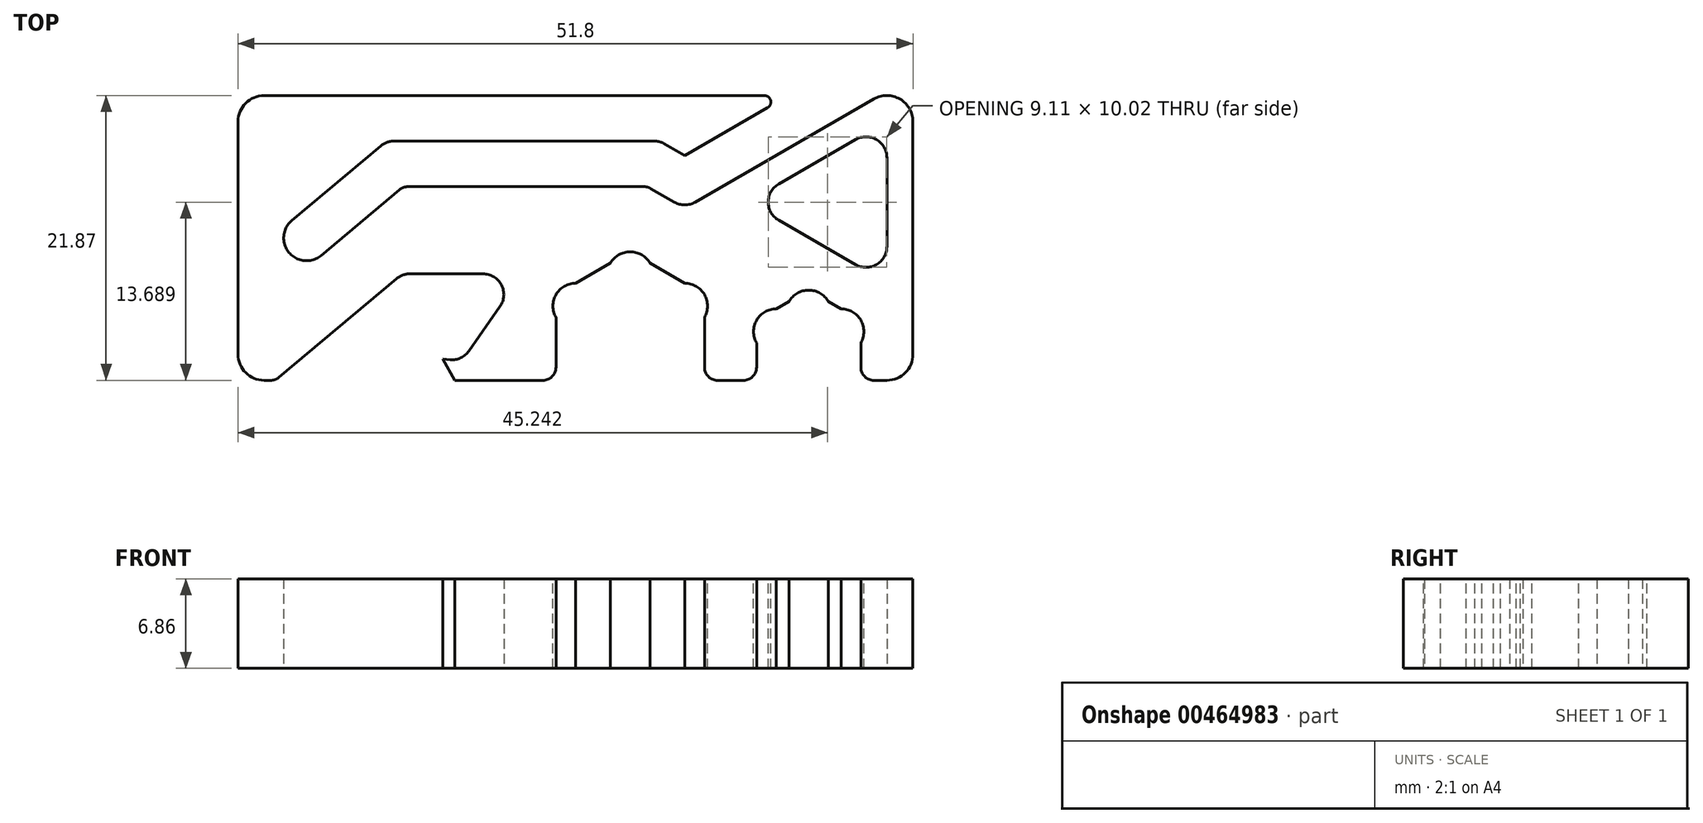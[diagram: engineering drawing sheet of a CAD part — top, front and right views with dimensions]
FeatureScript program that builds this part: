
annotation { "Feature Type Name" : "Feature", "Feature Type Description" : "" }
export const myFeature = defineFeature(function(context is Context, id is Id, definition is map)
    precondition{}
    {
        {
            var Q0;
            Q0=qCreatedBy(makeId("Top.planeOp"),FACE);
            var sketch = newSketch(context, id + "F0", { "sketchPlane" : qUnion([Q0])});
            skLineSegment(sketch, "E0", {"start": v(2, 0) * mm, "end": v(2.5, 0) * mm});
            skLineSegment(sketch, "E1", {"start": v(3.14, 0.23) * mm, "end": v(12.61, 8.18) * mm});
            skLineSegment(sketch, "E2", {"start": v(12.61, 8.18) * mm, "end": v(18.8, 8.18) * mm});
            skLineSegment(sketch, "E3", {"start": v(24.4, 0) * mm, "end": v(16.64, 0) * mm});
            skLineSegment(sketch, "E4", {"start": v(16.64, 0) * mm, "end": v(15.7, 1.63) * mm});
            skLineSegment(sketch, "E5", {"start": v(15.7, 1.63) * mm, "end": v(17.2, 1.5) * mm});
            skLineSegment(sketch, "E6", {"start": v(17.2, 1.5) * mm, "end": v(20.1, 5.66) * mm});
            skArc(sketch, "E7", {"start": v(20.1, 5.66) * mm, "mid": v(20.22, 7.32) * mm, "end": v(18.8, 8.18) * mm});
            skLineSegment(sketch, "E8", {"start": v(24.4, 0) * mm, "end": v(24.4, 6.58) * mm});
            skLineSegment(sketch, "E9", {"start": v(24.4, 6.58) * mm, "end": v(30.1, 9.87) * mm});
            skLineSegment(sketch, "E10", {"start": v(30.1, 9.87) * mm, "end": v(35.8, 6.58) * mm});
            skLineSegment(sketch, "E11", {"start": v(35.8, 6.58) * mm, "end": v(35.8, 0) * mm});
            skCircle(sketch, "E12", {"center": v(30.1, 3.3) * mm, "radius": 5.7 * mm, "construction": true});
            skLineSegment(sketch, "E13", {"start": v(18.8, 6.58) * mm, "end": v(20.4, 6.58) * mm, "construction": true});
            skArc(sketch, "E14", {"start": v(2.5, 0) * mm, "mid": v(2.84, 0.06) * mm, "end": v(3.14, 0.23) * mm});
            skLineSegment(sketch, "E15", {"start": v(0, 2) * mm, "end": v(0, 21.87) * mm});
            skArc(sketch, "E16", {"start": v(0, 2) * mm, "mid": v(0.59, 0.59) * mm, "end": v(2, 0) * mm});
            skLineSegment(sketch, "E17", {"start": v(35.8, 0) * mm, "end": v(39.8, 0) * mm});
            skLineSegment(sketch, "E18", {"start": v(39.8, 0) * mm, "end": v(39.8, 4.62) * mm});
            skLineSegment(sketch, "E19", {"start": v(39.8, 4.62) * mm, "end": v(43.8, 6.93) * mm});
            skLineSegment(sketch, "E20", {"start": v(43.8, 6.93) * mm, "end": v(47.8, 4.62) * mm});
            skLineSegment(sketch, "E21", {"start": v(47.8, 4.62) * mm, "end": v(47.8, 0) * mm});
            skLineSegment(sketch, "E22", {"start": v(47.8, 0) * mm, "end": v(51.8, 0) * mm});
            skCircle(sketch, "E23", {"center": v(43.8, 2.3) * mm, "radius": 4 * mm, "construction": true});
            skLineSegment(sketch, "E24", {"start": v(39.09, 13.69) * mm, "end": v(49.8, 7.5) * mm});
            skLineSegment(sketch, "E25", {"start": v(49.8, 7.5) * mm, "end": v(49.8, 19.87) * mm});
            skLineSegment(sketch, "E26", {"start": v(49.8, 19.87) * mm, "end": v(39.09, 13.69) * mm});
            skLineSegment(sketch, "E27", {"start": v(51.8, 0) * mm, "end": v(51.8, 19.87) * mm});
            skLineSegment(sketch, "E28", {"start": v(6.37, 9.6) * mm, "end": v(12.66, 14.87) * mm});
            skLineSegment(sketch, "E29", {"start": v(12.66, 14.87) * mm, "end": v(30.1, 14.87) * mm});
            skArc(sketch, "E30", {"start": v(4.13, 12.28) * mm, "mid": v(3.9, 9.81) * mm, "end": v(6.37, 9.6) * mm});
            skLineSegment(sketch, "E31", {"start": v(4.13, 12.28) * mm, "end": v(11.39, 18.37) * mm});
            skPoint(sketch, "E32", {"position": v(3.5, 10.94) * mm});
            skLineSegment(sketch, "E33", {"start": v(11.39, 18.37) * mm, "end": v(32.37, 18.37) * mm});
            skLineSegment(sketch, "E34", {"start": v(30.1, 14.87) * mm, "end": v(31.44, 14.87) * mm});
            skLineSegment(sketch, "E35", {"start": v(31.44, 14.87) * mm, "end": v(34.29, 13.23) * mm});
            skLineSegment(sketch, "E36", {"start": v(34.29, 13.23) * mm, "end": v(48.8, 21.6) * mm});
            skLineSegment(sketch, "E37", {"start": v(42.26, 21.87) * mm, "end": v(34.29, 17.27) * mm});
            skLineSegment(sketch, "E38", {"start": v(34.29, 17.27) * mm, "end": v(32.37, 18.37) * mm});
            skLineSegment(sketch, "E39", {"start": v(42.26, 21.87) * mm, "end": v(0, 21.87) * mm});
            skLineSegment(sketch, "E40", {"start": v(0, 0) * mm, "end": v(0, 21.87) * mm, "construction": true});
            skPoint(sketch, "E41", {"position": v(0, 10.94) * mm});
            skArc(sketch, "E42", {"start": v(51.8, 19.87) * mm, "mid": v(50.8, 21.6) * mm, "end": v(48.8, 21.6) * mm});
            skSolve(sketch);
        }
        {
            var Q0;
            Q0=makeQuery(id+"F0.imprint","IMPRINT",FACE,{"disambiguationData":[TD([[makeQuery(id+"F0.imprint","IMPRINT",EDGE,{"derivedFrom":sQuery(id+"F0.wireOp",EDGE,"E0")}),1.0]])]});
            extrude(context, id + "F1", {"entities" : qUnion([Q0]), "depth" : 6.86 * mm});
        }
        {
            var Q0;
            Q0=makeQuery(id+"F1.opExtrude","CAP_FACE",FACE,{"disambiguationData":[OSD([sQuery(id+"F0.wireOp",EDGE,"E0"),sQuery(id+"F0.wireOp",EDGE,"E1"),sQuery(id+"F0.wireOp",EDGE,"E2"),sQuery(id+"F0.wireOp",EDGE,"E3"),sQuery(id+"F0.wireOp",EDGE,"E4"),sQuery(id+"F0.wireOp",EDGE,"E5"),sQuery(id+"F0.wireOp",EDGE,"E6"),sQuery(id+"F0.wireOp",EDGE,"E7"),sQuery(id+"F0.wireOp",EDGE,"E8"),sQuery(id+"F0.wireOp",EDGE,"E9"),sQuery(id+"F0.wireOp",EDGE,"E10"),sQuery(id+"F0.wireOp",EDGE,"E11"),sQuery(id+"F0.wireOp",EDGE,"E14"),sQuery(id+"F0.wireOp",EDGE,"E15"),sQuery(id+"F0.wireOp",EDGE,"E16"),sQuery(id+"F0.wireOp",EDGE,"E17"),sQuery(id+"F0.wireOp",EDGE,"E18"),sQuery(id+"F0.wireOp",EDGE,"E19"),sQuery(id+"F0.wireOp",EDGE,"E20"),sQuery(id+"F0.wireOp",EDGE,"E21"),sQuery(id+"F0.wireOp",EDGE,"E22"),sQuery(id+"F0.wireOp",EDGE,"E24"),sQuery(id+"F0.wireOp",EDGE,"E25"),sQuery(id+"F0.wireOp",EDGE,"E26"),sQuery(id+"F0.wireOp",EDGE,"E27"),sQuery(id+"F0.wireOp",EDGE,"E28"),sQuery(id+"F0.wireOp",EDGE,"E29"),sQuery(id+"F0.wireOp",EDGE,"E30"),sQuery(id+"F0.wireOp",EDGE,"E31"),sQuery(id+"F0.wireOp",EDGE,"E33"),sQuery(id+"F0.wireOp",EDGE,"E34"),sQuery(id+"F0.wireOp",EDGE,"E35"),sQuery(id+"F0.wireOp",EDGE,"E36"),sQuery(id+"F0.wireOp",EDGE,"E37"),sQuery(id+"F0.wireOp",EDGE,"E38"),sQuery(id+"F0.wireOp",EDGE,"E39"),sQuery(id+"F0.wireOp",EDGE,"E42")])],"isStart":false});
            var sketch = newSketch(context, id + "F2", { "sketchPlane" : qUnion([Q0])});
            skLineSegment(sketch, "E43", {"start": v(30.1, 9.87) * mm, "end": v(30.1, 3.3) * mm, "construction": true});
            skLineSegment(sketch, "E44", {"start": v(30.1, 3.3) * mm, "end": v(24.4, 6.58) * mm, "construction": true});
            skLineSegment(sketch, "E45", {"start": v(30.1, 3.3) * mm, "end": v(35.8, 6.58) * mm, "construction": true});
            skCircle(sketch, "E46", {"center": v(30.1, 8.12) * mm, "radius": 1.75 * mm});
            skCircle(sketch, "E47", {"center": v(34.28, 5.7) * mm, "radius": 1.75 * mm});
            skCircle(sketch, "E48", {"center": v(25.91, 5.7) * mm, "radius": 1.75 * mm});
            skLineSegment(sketch, "E49", {"start": v(43.8, 6.93) * mm, "end": v(43.8, 2.3) * mm, "construction": true});
            skLineSegment(sketch, "E50", {"start": v(43.8, 2.3) * mm, "end": v(39.8, 4.62) * mm, "construction": true});
            skLineSegment(sketch, "E51", {"start": v(43.8, 2.3) * mm, "end": v(47.8, 4.62) * mm, "construction": true});
            skCircle(sketch, "E52", {"center": v(43.8, 5.18) * mm, "radius": 1.75 * mm});
            skCircle(sketch, "E53", {"center": v(46.28, 3.74) * mm, "radius": 1.75 * mm});
            skCircle(sketch, "E54", {"center": v(41.31, 3.74) * mm, "radius": 1.75 * mm});
            skLineSegment(sketch, "E55", {"start": v(21.88, 18.37) * mm, "end": v(21.88, 14.87) * mm, "construction": true});
            skLineSegment(sketch, "E56", {"start": v(28.35, 8.12) * mm, "end": v(31.85, 8.12) * mm, "construction": true});
            skSolve(sketch);
        }
        {
            var Q0;
            Q0=qSketchRegion(id+"F2",true);
            extrude(context, id + "F3", {"entities" : qUnion([Q0]), "operationType" : NewBodyOperationType.REMOVE, "endBound" : BoundingType.THROUGH_ALL, "oppositeDirection" : true, "depth" : 25 * mm});
        }
        {
            var Q0;
            Q0=makeQuery(id+"F1.opExtrude","SWEPT_EDGE",EDGE,{"disambiguationData":[OSD([sQuery(id+"F0.wireOp",EDGE,"E3"),sQuery(id+"F0.wireOp",EDGE,"E8")])]});
            var Q1;
            Q1=makeQuery(id+"F1.opExtrude","SWEPT_EDGE",EDGE,{"disambiguationData":[OSD([sQuery(id+"F0.wireOp",EDGE,"E11"),sQuery(id+"F0.wireOp",EDGE,"E17")])]});
            var Q2;
            Q2=makeQuery(id+"F1.opExtrude","SWEPT_EDGE",EDGE,{"disambiguationData":[OSD([sQuery(id+"F0.wireOp",EDGE,"E17"),sQuery(id+"F0.wireOp",EDGE,"E18")])]});
            var Q3;
            Q3=makeQuery(id+"F1.opExtrude","SWEPT_EDGE",EDGE,{"disambiguationData":[OSD([sQuery(id+"F0.wireOp",EDGE,"E21"),sQuery(id+"F0.wireOp",EDGE,"E22")])]});
            fillet(context, id + "F4", {"entities" : qUnion([Q0, Q1, Q2, Q3]), "radius" : 1 * mm, "tangentPropagation" : true, "allowEdgeOverflow" : false});
        }
        {
            var Q0;
            Q0=makeQuery(id+"F1.opExtrude","SWEPT_EDGE",EDGE,{"disambiguationData":[OSD([sQuery(id+"F0.wireOp",EDGE,"E22"),sQuery(id+"F0.wireOp",EDGE,"E27")])]});
            var Q1;
            Q1=makeQuery(id+"F1.opExtrude","SWEPT_EDGE",EDGE,{"disambiguationData":[OSD([sQuery(id+"F0.wireOp",EDGE,"E15"),sQuery(id+"F0.wireOp",EDGE,"E39")])]});
            fillet(context, id + "F5", {"entities" : qUnion([Q0, Q1]), "radius" : 2 * mm, "tangentPropagation" : true, "allowEdgeOverflow" : false});
        }
        {
            var Q0;
            Q0=makeQuery(id+"F1.opExtrude","SWEPT_EDGE",EDGE,{"disambiguationData":[OSD([sQuery(id+"F0.wireOp",EDGE,"E37"),sQuery(id+"F0.wireOp",EDGE,"E39")])]});
            fillet(context, id + "F6", {"entities" : qUnion([Q0]), "radius" : 0.5 * mm, "tangentPropagation" : true, "allowEdgeOverflow" : false});
        }
        {
            var Q0;
            Q0=makeQuery(id+"F1.opExtrude","SWEPT_EDGE",EDGE,{"disambiguationData":[OSD([sQuery(id+"F0.wireOp",EDGE,"E28"),sQuery(id+"F0.wireOp",EDGE,"E29")])]});
            var Q1;
            Q1=makeQuery(id+"F1.opExtrude","SWEPT_EDGE",EDGE,{"disambiguationData":[OSD([sQuery(id+"F0.wireOp",EDGE,"E34"),sQuery(id+"F0.wireOp",EDGE,"E35")])]});
            fillet(context, id + "F7", {"entities" : qUnion([Q0, Q1]), "radius" : 1 * mm, "tangentPropagation" : true, "allowEdgeOverflow" : false});
        }
        {
            var Q0;
            Q0=makeQuery(id+"F1.opExtrude","SWEPT_EDGE",EDGE,{"disambiguationData":[OSD([sQuery(id+"F0.wireOp",EDGE,"E24"),sQuery(id+"F0.wireOp",EDGE,"E26")])]});
            var Q1;
            Q1=makeQuery(id+"F1.opExtrude","SWEPT_EDGE",EDGE,{"disambiguationData":[OSD([sQuery(id+"F0.wireOp",EDGE,"E25"),sQuery(id+"F0.wireOp",EDGE,"E26")])]});
            var Q2;
            Q2=makeQuery(id+"F1.opExtrude","SWEPT_EDGE",EDGE,{"disambiguationData":[OSD([sQuery(id+"F0.wireOp",EDGE,"E24"),sQuery(id+"F0.wireOp",EDGE,"E25")])]});
            fillet(context, id + "F8", {"entities" : qUnion([Q0, Q1, Q2]), "radius" : 1.6 * mm, "tangentPropagation" : true, "allowEdgeOverflow" : false});
        }
        {
            var Q0;
            Q0=makeQuery(id+"F1.opExtrude","SWEPT_EDGE",EDGE,{"disambiguationData":[OSD([sQuery(id+"F0.wireOp",EDGE,"E5"),sQuery(id+"F0.wireOp",EDGE,"E6")])]});
            fillet(context, id + "F9", {"entities" : qUnion([Q0]), "radius" : 1.6 * mm, "tangentPropagation" : true, "allowEdgeOverflow" : false});
        }
        {
            var Q0;
            Q0=makeQuery(id+"F1.opExtrude","SWEPT_EDGE",EDGE,{"disambiguationData":[OSD([sQuery(id+"F0.wireOp",EDGE,"E35"),sQuery(id+"F0.wireOp",EDGE,"E36")])]});
            var Q1;
            Q1=makeQuery(id+"F1.opExtrude","SWEPT_EDGE",EDGE,{"disambiguationData":[OSD([sQuery(id+"F0.wireOp",EDGE,"E33"),sQuery(id+"F0.wireOp",EDGE,"E38")])]});
            var Q2;
            Q2=makeQuery(id+"F1.opExtrude","SWEPT_EDGE",EDGE,{"disambiguationData":[OSD([sQuery(id+"F0.wireOp",EDGE,"E31"),sQuery(id+"F0.wireOp",EDGE,"E33")])]});
            var Q3;
            Q3=makeQuery(id+"F1.opExtrude","SWEPT_EDGE",EDGE,{"disambiguationData":[OSD([sQuery(id+"F0.wireOp",EDGE,"E1"),sQuery(id+"F0.wireOp",EDGE,"E2")])]});
            fillet(context, id + "F10", {"entities" : qUnion([Q0, Q1, Q2, Q3]), "radius" : 1.6 * mm, "tangentPropagation" : true, "allowEdgeOverflow" : false});
        }
    });
